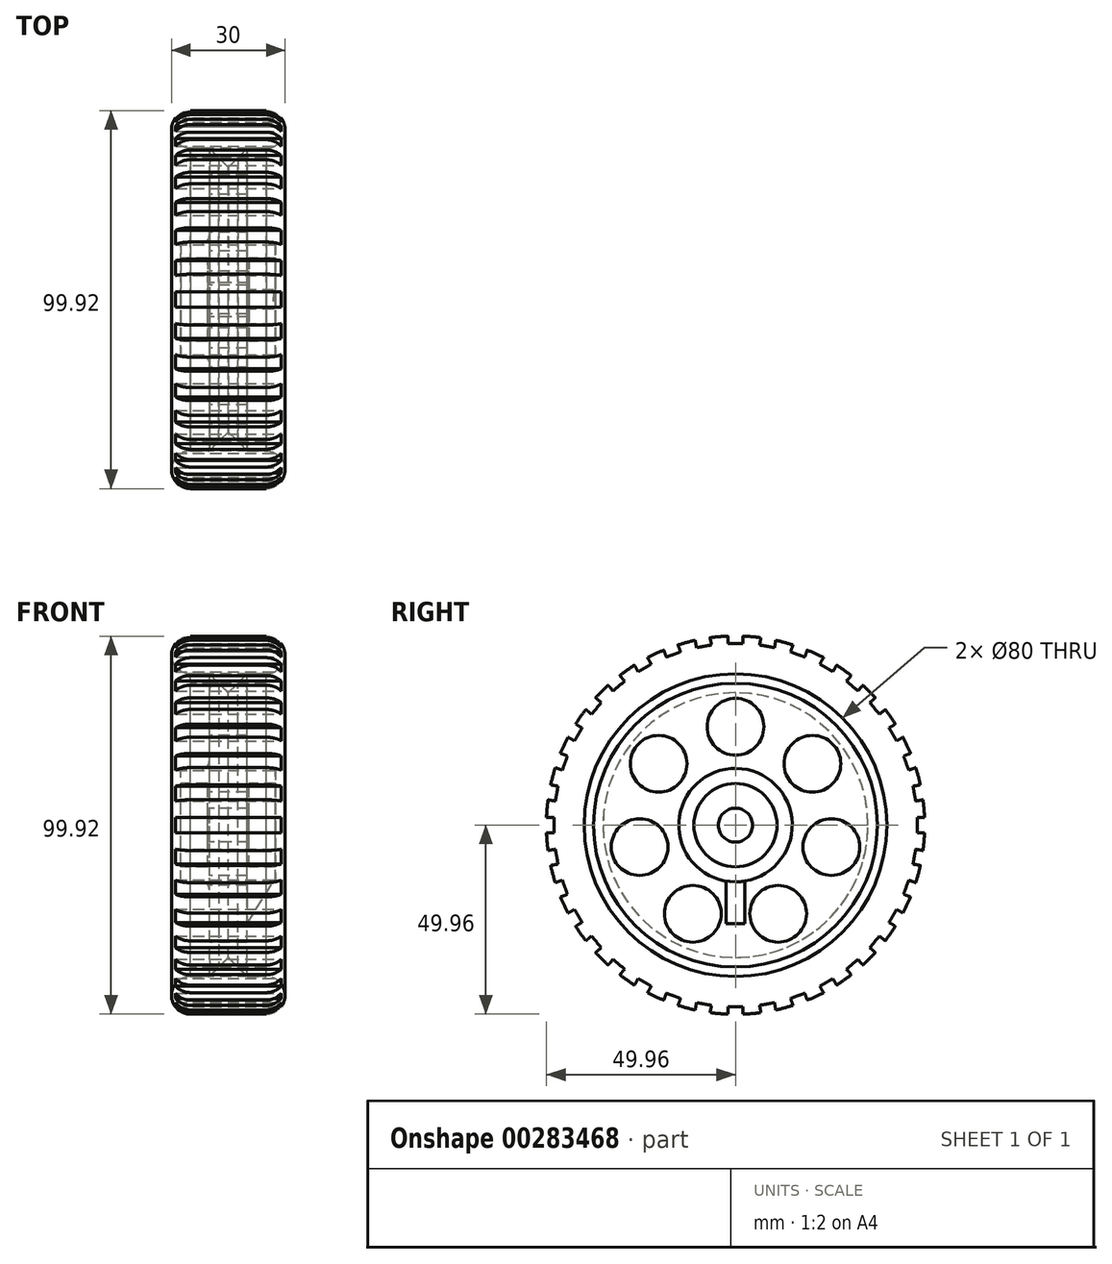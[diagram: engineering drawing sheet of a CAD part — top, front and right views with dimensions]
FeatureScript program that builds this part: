
annotation { "Feature Type Name" : "Feature", "Feature Type Description" : "" }
export const myFeature = defineFeature(function(context is Context, id is Id, definition is map)
    precondition{}
    {
        {
            var Q0;
            Q0=qCreatedBy(makeId("Right.planeOp"),FACE);
            var sketch = newSketch(context, id + "F0", { "sketchPlane" : qUnion([Q0])});
            skCircle(sketch, "E0", {"center": v(0, 0) * mm, "radius": 4.5 * mm});
            skCircle(sketch, "E1", {"center": v(0, 0) * mm, "radius": 11 * mm});
            skCircle(sketch, "E2", {"center": v(0, 0) * mm, "radius": 15 * mm});
            skCircle(sketch, "E3", {"center": v(0, 0) * mm, "radius": 37.5 * mm});
            skCircle(sketch, "E4", {"center": v(0, 0) * mm, "radius": 40 * mm});
            skCircle(sketch, "E5", {"center": v(0, 26) * mm, "radius": 7.5 * mm});
            skCircle(sketch, "E6.1.0", {"center": v(-20.33, 16.21) * mm, "radius": 7.5 * mm});
            skCircle(sketch, "E6.2.0", {"center": v(-25.35, -5.79) * mm, "radius": 7.5 * mm});
            skCircle(sketch, "E6.3.0", {"center": v(-11.28, -23.43) * mm, "radius": 7.5 * mm});
            skCircle(sketch, "E6.4.0", {"center": v(11.28, -23.43) * mm, "radius": 7.5 * mm});
            skCircle(sketch, "E7.1.5.0", {"center": v(25.35, -5.79) * mm, "radius": 7.5 * mm});
            skCircle(sketch, "E7.1.6.0", {"center": v(20.33, 16.21) * mm, "radius": 7.5 * mm});
            skCircle(sketch, "E8", {"center": v(0, 0) * mm, "radius": 26 * mm, "construction": true});
            skPoint(sketch, "E9", {"position": v(0, -26) * mm});
            skSolve(sketch);
        }
        {
            var Q0;
            Q0=makeQuery(id+"F0.imprint","IMPRINT",FACE,{"disambiguationData":[TD([[makeQuery(id+"F0.imprint","IMPRINT",EDGE,{"derivedFrom":sQuery(id+"F0.wireOp",EDGE,"E1")}),-1.0]])]});
            extrude(context, id + "F1", {"entities" : qUnion([Q0]), "endBound" : BoundingType.SYMMETRIC, "depth" : 25 * mm, "hasSecondDirection" : true, "secondDirectionOppositeDirection" : true, "secondDirectionDepth" : 10 * mm});
        }
        {
            var Q0;
            Q0=makeQuery(id+"F0.imprint","IMPRINT",FACE,{"disambiguationData":[TD([[makeQuery(id+"F0.imprint","IMPRINT",EDGE,{"derivedFrom":sQuery(id+"F0.wireOp",EDGE,"E3")}),-1.0]])]});
            extrude(context, id + "F2", {"entities" : qUnion([Q0]), "endBound" : BoundingType.SYMMETRIC, "depth" : 20 * mm});
        }
        {
            var Q0;
            Q0=makeQuery(id+"F0.imprint","IMPRINT",FACE,{"disambiguationData":[TD([[makeQuery(id+"F0.imprint","IMPRINT",EDGE,{"derivedFrom":sQuery(id+"F0.wireOp",EDGE,"E2")}),-1.0]])]});
            extrude(context, id + "F3", {"entities" : qUnion([Q0]), "depth" : 5 * mm, "hasSecondDirection" : true, "secondDirectionOppositeDirection" : true, "secondDirectionDepth" : 5 * mm});
        }
        {
            var Q0;
            Q0=makeQuery(id+"F0.imprint","IMPRINT",FACE,{"disambiguationData":[TD([[makeQuery(id+"F0.imprint","IMPRINT",EDGE,{"derivedFrom":sQuery(id+"F0.wireOp",EDGE,"E0")}),-1.0]])]});
            extrude(context, id + "F4", {"entities" : qUnion([Q0]), "operationType" : NewBodyOperationType.ADD, "endBound" : BoundingType.SYMMETRIC, "depth" : (25 - 14) * mm, "hasSecondDirection" : true, "secondDirectionOppositeDirection" : true, "secondDirectionDepth" : 3 * mm});
        }
        {
            var Q0;
            Q0=qCreatedBy(makeId("Front.planeOp"),FACE);
            var sketch = newSketch(context, id + "F5", { "sketchPlane" : qUnion([Q0])});
            skLineSegment(sketch, "E10", {"start": v(10, 50) * mm, "end": v(-10, 50) * mm});
            skArc(sketch, "E11", {"start": v(10, 50) * mm, "mid": v(15, 45) * mm, "end": v(10, 40) * mm});
            skArc(sketch, "E12", {"start": v(-10, 50) * mm, "mid": v(-15, 45) * mm, "end": v(-10, 40) * mm});
            skLineSegment(sketch, "E13", {"start": v(10, 40) * mm, "end": v(5, 40) * mm});
            skLineSegment(sketch, "E14", {"start": v(5, 40) * mm, "end": v(0, 35) * mm});
            skLineSegment(sketch, "E15", {"start": v(0, 35) * mm, "end": v(-5, 40) * mm});
            skLineSegment(sketch, "E16", {"start": v(-5, 40) * mm, "end": v(-10, 40) * mm});
            skLineSegment(sketch, "E17", {"start": v(15.37, 0) * mm, "end": v(-22.9, 0) * mm, "construction": true});
            skSolve(sketch);
        }
        {
            var Q0;
            Q0=makeQuery(id+"F5.imprint","IMPRINT",FACE,{"disambiguationData":[TD([[makeQuery(id+"F5.imprint","IMPRINT",EDGE,{"derivedFrom":sQuery(id+"F5.wireOp",EDGE,"E10")}),1.0]])]});
            var Q1;
            Q1=sQuery(id+"F5.wireOp",EDGE,"E17");
            revolve(context, id + "F6", {"entities" : qUnion([Q0]), "axis" : qUnion([Q1]), "revolveType" : RevolveType.FULL});
        }
        {
            var Q0;
            Q0=makeQuery(id+"F6.opRevolve","SWEPT_BODY",BODY,{"disambiguationData":[OSD([sQuery(id+"F5.wireOp",EDGE,"E10"),sQuery(id+"F5.wireOp",EDGE,"E11"),sQuery(id+"F5.wireOp",EDGE,"E12"),sQuery(id+"F5.wireOp",EDGE,"E13"),sQuery(id+"F5.wireOp",EDGE,"E14"),sQuery(id+"F5.wireOp",EDGE,"E15"),sQuery(id+"F5.wireOp",EDGE,"E16")])]});
            var Q1;
            Q1=makeQuery(id+"F3.opExtrude","SWEPT_BODY",BODY,{"disambiguationData":[OSD([sQuery(id+"F0.wireOp",EDGE,"E2"),sQuery(id+"F0.wireOp",EDGE,"E3"),sQuery(id+"F0.wireOp",EDGE,"E5"),sQuery(id+"F0.wireOp",EDGE,"E6.1.0"),sQuery(id+"F0.wireOp",EDGE,"E6.2.0"),sQuery(id+"F0.wireOp",EDGE,"E6.3.0"),sQuery(id+"F0.wireOp",EDGE,"E6.4.0"),sQuery(id+"F0.wireOp",EDGE,"E7.1.5.0"),sQuery(id+"F0.wireOp",EDGE,"E7.1.6.0")])]});
            booleanBodies(context, id + "F7", {"operationType" : BooleanOperationType.SUBTRACTION, "tools" : qUnion([Q0]), "targets" : qUnion([Q1]), "keepTools" : true});
        }
        {
            var Q0;
            Q0=qCreatedBy(makeId("Right.planeOp"),FACE);
            var sketch = newSketch(context, id + "F8", { "sketchPlane" : qUnion([Q0])});
            skLineSegment(sketch, "E18.bottom", {"start": v(2, 52) * mm, "end": v(-2, 52) * mm});
            skLineSegment(sketch, "E18.top", {"start": v(2, 48) * mm, "end": v(-2, 48) * mm});
            skLineSegment(sketch, "E18.left", {"start": v(2, 52) * mm, "end": v(2, 48) * mm});
            skLineSegment(sketch, "E18.right", {"start": v(-2, 52) * mm, "end": v(-2, 48) * mm});
            skPoint(sketch, "E18.middle", {"position": v(0, 50) * mm});
            skLineSegment(sketch, "E19.1.0", {"start": v(-7.06, 51.56) * mm, "end": v(-11, 50.86) * mm});
            skLineSegment(sketch, "E19.1.1", {"start": v(-7.06, 51.56) * mm, "end": v(-6.37, 47.62) * mm});
            skLineSegment(sketch, "E19.1.2", {"start": v(-6.37, 47.62) * mm, "end": v(-10.3, 46.92) * mm});
            skLineSegment(sketch, "E19.1.3", {"start": v(-11, 50.86) * mm, "end": v(-10.3, 46.92) * mm});
            skLineSegment(sketch, "E19.2.0", {"start": v(-15.9, 49.55) * mm, "end": v(-19.66, 48.18) * mm});
            skLineSegment(sketch, "E19.2.1", {"start": v(-15.9, 49.55) * mm, "end": v(-14.54, 45.79) * mm});
            skLineSegment(sketch, "E19.2.2", {"start": v(-14.54, 45.79) * mm, "end": v(-18.3, 44.42) * mm});
            skLineSegment(sketch, "E19.2.3", {"start": v(-19.66, 48.18) * mm, "end": v(-18.3, 44.42) * mm});
            skLineSegment(sketch, "E19.3.0", {"start": v(-24.27, 46.03) * mm, "end": v(-27.73, 44.03) * mm});
            skLineSegment(sketch, "E19.3.1", {"start": v(-24.27, 46.03) * mm, "end": v(-22.27, 42.57) * mm});
            skLineSegment(sketch, "E19.3.2", {"start": v(-22.27, 42.57) * mm, "end": v(-25.73, 40.57) * mm});
            skLineSegment(sketch, "E19.3.3", {"start": v(-27.73, 44.03) * mm, "end": v(-25.73, 40.57) * mm});
            skLineSegment(sketch, "E19.4.0", {"start": v(-31.9, 41.12) * mm, "end": v(-34.96, 38.55) * mm});
            skLineSegment(sketch, "E19.4.1", {"start": v(-31.9, 41.12) * mm, "end": v(-29.32, 38.06) * mm});
            skLineSegment(sketch, "E19.4.2", {"start": v(-29.32, 38.06) * mm, "end": v(-32.39, 35.48) * mm});
            skLineSegment(sketch, "E19.4.3", {"start": v(-34.96, 38.55) * mm, "end": v(-32.39, 35.48) * mm});
            skLineSegment(sketch, "E19.5.0", {"start": v(-38.55, 34.96) * mm, "end": v(-41.12, 31.9) * mm});
            skLineSegment(sketch, "E19.5.1", {"start": v(-38.55, 34.96) * mm, "end": v(-35.48, 32.39) * mm});
            skLineSegment(sketch, "E19.5.2", {"start": v(-35.48, 32.39) * mm, "end": v(-38.06, 29.32) * mm});
            skLineSegment(sketch, "E19.5.3", {"start": v(-41.12, 31.9) * mm, "end": v(-38.06, 29.32) * mm});
            skLineSegment(sketch, "E19.6.0", {"start": v(-44.03, 27.73) * mm, "end": v(-46.03, 24.27) * mm});
            skLineSegment(sketch, "E19.6.1", {"start": v(-44.03, 27.73) * mm, "end": v(-40.57, 25.73) * mm});
            skLineSegment(sketch, "E19.6.2", {"start": v(-40.57, 25.73) * mm, "end": v(-42.57, 22.27) * mm});
            skLineSegment(sketch, "E19.6.3", {"start": v(-46.03, 24.27) * mm, "end": v(-42.57, 22.27) * mm});
            skLineSegment(sketch, "E19.7.0", {"start": v(-48.18, 19.66) * mm, "end": v(-49.55, 15.9) * mm});
            skLineSegment(sketch, "E19.7.1", {"start": v(-48.18, 19.66) * mm, "end": v(-44.42, 18.3) * mm});
            skLineSegment(sketch, "E19.7.2", {"start": v(-44.42, 18.3) * mm, "end": v(-45.79, 14.54) * mm});
            skLineSegment(sketch, "E19.7.3", {"start": v(-49.55, 15.9) * mm, "end": v(-45.79, 14.54) * mm});
            skLineSegment(sketch, "E19.8.0", {"start": v(-50.86, 11) * mm, "end": v(-51.56, 7.06) * mm});
            skLineSegment(sketch, "E19.8.1", {"start": v(-50.86, 11) * mm, "end": v(-46.92, 10.3) * mm});
            skLineSegment(sketch, "E19.8.2", {"start": v(-46.92, 10.3) * mm, "end": v(-47.62, 6.37) * mm});
            skLineSegment(sketch, "E19.8.3", {"start": v(-51.56, 7.06) * mm, "end": v(-47.62, 6.37) * mm});
            skLineSegment(sketch, "E19.9.0", {"start": v(-52, 2) * mm, "end": v(-52, -2) * mm});
            skLineSegment(sketch, "E19.9.1", {"start": v(-52, 2) * mm, "end": v(-48, 2) * mm});
            skLineSegment(sketch, "E19.9.2", {"start": v(-48, 2) * mm, "end": v(-48, -2) * mm});
            skLineSegment(sketch, "E19.9.3", {"start": v(-52, -2) * mm, "end": v(-48, -2) * mm});
            skLineSegment(sketch, "E19.10.0", {"start": v(-51.56, -7.06) * mm, "end": v(-50.86, -11) * mm});
            skLineSegment(sketch, "E19.10.1", {"start": v(-51.56, -7.06) * mm, "end": v(-47.62, -6.37) * mm});
            skLineSegment(sketch, "E19.10.2", {"start": v(-47.62, -6.37) * mm, "end": v(-46.92, -10.3) * mm});
            skLineSegment(sketch, "E19.10.3", {"start": v(-50.86, -11) * mm, "end": v(-46.92, -10.3) * mm});
            skLineSegment(sketch, "E19.11.0", {"start": v(-49.55, -15.9) * mm, "end": v(-48.18, -19.66) * mm});
            skLineSegment(sketch, "E19.11.1", {"start": v(-49.55, -15.9) * mm, "end": v(-45.79, -14.54) * mm});
            skLineSegment(sketch, "E19.11.2", {"start": v(-45.79, -14.54) * mm, "end": v(-44.42, -18.3) * mm});
            skLineSegment(sketch, "E19.11.3", {"start": v(-48.18, -19.66) * mm, "end": v(-44.42, -18.3) * mm});
            skLineSegment(sketch, "E19.12.0", {"start": v(-46.03, -24.27) * mm, "end": v(-44.03, -27.73) * mm});
            skLineSegment(sketch, "E19.12.1", {"start": v(-46.03, -24.27) * mm, "end": v(-42.57, -22.27) * mm});
            skLineSegment(sketch, "E19.12.2", {"start": v(-42.57, -22.27) * mm, "end": v(-40.57, -25.73) * mm});
            skLineSegment(sketch, "E19.12.3", {"start": v(-44.03, -27.73) * mm, "end": v(-40.57, -25.73) * mm});
            skLineSegment(sketch, "E19.13.0", {"start": v(-41.12, -31.9) * mm, "end": v(-38.55, -34.96) * mm});
            skLineSegment(sketch, "E19.13.1", {"start": v(-41.12, -31.9) * mm, "end": v(-38.06, -29.32) * mm});
            skLineSegment(sketch, "E19.13.2", {"start": v(-38.06, -29.32) * mm, "end": v(-35.48, -32.39) * mm});
            skLineSegment(sketch, "E19.13.3", {"start": v(-38.55, -34.96) * mm, "end": v(-35.48, -32.39) * mm});
            skLineSegment(sketch, "E19.14.0", {"start": v(-34.96, -38.55) * mm, "end": v(-31.9, -41.12) * mm});
            skLineSegment(sketch, "E19.14.1", {"start": v(-34.96, -38.55) * mm, "end": v(-32.39, -35.48) * mm});
            skLineSegment(sketch, "E19.14.2", {"start": v(-32.39, -35.48) * mm, "end": v(-29.32, -38.06) * mm});
            skLineSegment(sketch, "E19.14.3", {"start": v(-31.9, -41.12) * mm, "end": v(-29.32, -38.06) * mm});
            skLineSegment(sketch, "E19.15.0", {"start": v(-27.73, -44.03) * mm, "end": v(-24.27, -46.03) * mm});
            skLineSegment(sketch, "E19.15.1", {"start": v(-27.73, -44.03) * mm, "end": v(-25.73, -40.57) * mm});
            skLineSegment(sketch, "E19.15.2", {"start": v(-25.73, -40.57) * mm, "end": v(-22.27, -42.57) * mm});
            skLineSegment(sketch, "E19.15.3", {"start": v(-24.27, -46.03) * mm, "end": v(-22.27, -42.57) * mm});
            skLineSegment(sketch, "E19.16.0", {"start": v(-19.66, -48.18) * mm, "end": v(-15.9, -49.55) * mm});
            skLineSegment(sketch, "E19.16.1", {"start": v(-19.66, -48.18) * mm, "end": v(-18.3, -44.42) * mm});
            skLineSegment(sketch, "E19.16.2", {"start": v(-18.3, -44.42) * mm, "end": v(-14.54, -45.79) * mm});
            skLineSegment(sketch, "E19.16.3", {"start": v(-15.9, -49.55) * mm, "end": v(-14.54, -45.79) * mm});
            skLineSegment(sketch, "E19.17.0", {"start": v(-11, -50.86) * mm, "end": v(-7.06, -51.56) * mm});
            skLineSegment(sketch, "E19.17.1", {"start": v(-11, -50.86) * mm, "end": v(-10.3, -46.92) * mm});
            skLineSegment(sketch, "E19.17.2", {"start": v(-10.3, -46.92) * mm, "end": v(-6.37, -47.62) * mm});
            skLineSegment(sketch, "E19.17.3", {"start": v(-7.06, -51.56) * mm, "end": v(-6.37, -47.62) * mm});
            skLineSegment(sketch, "E19.18.0", {"start": v(-2, -52) * mm, "end": v(2, -52) * mm});
            skLineSegment(sketch, "E19.18.1", {"start": v(-2, -52) * mm, "end": v(-2, -48) * mm});
            skLineSegment(sketch, "E19.18.2", {"start": v(-2, -48) * mm, "end": v(2, -48) * mm});
            skLineSegment(sketch, "E19.18.3", {"start": v(2, -52) * mm, "end": v(2, -48) * mm});
            skLineSegment(sketch, "E19.19.0", {"start": v(7.06, -51.56) * mm, "end": v(11, -50.86) * mm});
            skLineSegment(sketch, "E19.19.1", {"start": v(7.06, -51.56) * mm, "end": v(6.37, -47.62) * mm});
            skLineSegment(sketch, "E19.19.2", {"start": v(6.37, -47.62) * mm, "end": v(10.3, -46.92) * mm});
            skLineSegment(sketch, "E19.19.3", {"start": v(11, -50.86) * mm, "end": v(10.3, -46.92) * mm});
            skLineSegment(sketch, "E19.20.0", {"start": v(15.9, -49.55) * mm, "end": v(19.66, -48.18) * mm});
            skLineSegment(sketch, "E19.20.1", {"start": v(15.9, -49.55) * mm, "end": v(14.54, -45.79) * mm});
            skLineSegment(sketch, "E19.20.2", {"start": v(14.54, -45.79) * mm, "end": v(18.3, -44.42) * mm});
            skLineSegment(sketch, "E19.20.3", {"start": v(19.66, -48.18) * mm, "end": v(18.3, -44.42) * mm});
            skLineSegment(sketch, "E19.21.0", {"start": v(24.27, -46.03) * mm, "end": v(27.73, -44.03) * mm});
            skLineSegment(sketch, "E19.21.1", {"start": v(24.27, -46.03) * mm, "end": v(22.27, -42.57) * mm});
            skLineSegment(sketch, "E19.21.2", {"start": v(22.27, -42.57) * mm, "end": v(25.73, -40.57) * mm});
            skLineSegment(sketch, "E19.21.3", {"start": v(27.73, -44.03) * mm, "end": v(25.73, -40.57) * mm});
            skLineSegment(sketch, "E19.22.0", {"start": v(31.9, -41.12) * mm, "end": v(34.96, -38.55) * mm});
            skLineSegment(sketch, "E19.22.1", {"start": v(31.9, -41.12) * mm, "end": v(29.32, -38.06) * mm});
            skLineSegment(sketch, "E19.22.2", {"start": v(29.32, -38.06) * mm, "end": v(32.39, -35.48) * mm});
            skLineSegment(sketch, "E19.22.3", {"start": v(34.96, -38.55) * mm, "end": v(32.39, -35.48) * mm});
            skLineSegment(sketch, "E19.23.0", {"start": v(38.55, -34.96) * mm, "end": v(41.12, -31.9) * mm});
            skLineSegment(sketch, "E19.23.1", {"start": v(38.55, -34.96) * mm, "end": v(35.48, -32.39) * mm});
            skLineSegment(sketch, "E19.23.2", {"start": v(35.48, -32.39) * mm, "end": v(38.06, -29.32) * mm});
            skLineSegment(sketch, "E19.23.3", {"start": v(41.12, -31.9) * mm, "end": v(38.06, -29.32) * mm});
            skLineSegment(sketch, "E19.24.0", {"start": v(44.03, -27.73) * mm, "end": v(46.03, -24.27) * mm});
            skLineSegment(sketch, "E19.24.1", {"start": v(44.03, -27.73) * mm, "end": v(40.57, -25.73) * mm});
            skLineSegment(sketch, "E19.24.2", {"start": v(40.57, -25.73) * mm, "end": v(42.57, -22.27) * mm});
            skLineSegment(sketch, "E19.24.3", {"start": v(46.03, -24.27) * mm, "end": v(42.57, -22.27) * mm});
            skLineSegment(sketch, "E19.25.0", {"start": v(48.18, -19.66) * mm, "end": v(49.55, -15.9) * mm});
            skLineSegment(sketch, "E19.25.1", {"start": v(48.18, -19.66) * mm, "end": v(44.42, -18.3) * mm});
            skLineSegment(sketch, "E19.25.2", {"start": v(44.42, -18.3) * mm, "end": v(45.79, -14.54) * mm});
            skLineSegment(sketch, "E19.25.3", {"start": v(49.55, -15.9) * mm, "end": v(45.79, -14.54) * mm});
            skLineSegment(sketch, "E19.26.0", {"start": v(50.86, -11) * mm, "end": v(51.56, -7.06) * mm});
            skLineSegment(sketch, "E19.26.1", {"start": v(50.86, -11) * mm, "end": v(46.92, -10.3) * mm});
            skLineSegment(sketch, "E19.26.2", {"start": v(46.92, -10.3) * mm, "end": v(47.62, -6.37) * mm});
            skLineSegment(sketch, "E19.26.3", {"start": v(51.56, -7.06) * mm, "end": v(47.62, -6.37) * mm});
            skLineSegment(sketch, "E19.27.0", {"start": v(52, -2) * mm, "end": v(52, 2) * mm});
            skLineSegment(sketch, "E19.27.1", {"start": v(52, -2) * mm, "end": v(48, -2) * mm});
            skLineSegment(sketch, "E19.27.2", {"start": v(48, -2) * mm, "end": v(48, 2) * mm});
            skLineSegment(sketch, "E19.27.3", {"start": v(52, 2) * mm, "end": v(48, 2) * mm});
            skLineSegment(sketch, "E19.28.0", {"start": v(51.56, 7.06) * mm, "end": v(50.86, 11) * mm});
            skLineSegment(sketch, "E19.28.1", {"start": v(51.56, 7.06) * mm, "end": v(47.62, 6.37) * mm});
            skLineSegment(sketch, "E19.28.2", {"start": v(47.62, 6.37) * mm, "end": v(46.92, 10.3) * mm});
            skLineSegment(sketch, "E19.28.3", {"start": v(50.86, 11) * mm, "end": v(46.92, 10.3) * mm});
            skLineSegment(sketch, "E19.29.0", {"start": v(49.55, 15.9) * mm, "end": v(48.18, 19.66) * mm});
            skLineSegment(sketch, "E19.29.1", {"start": v(49.55, 15.9) * mm, "end": v(45.79, 14.54) * mm});
            skLineSegment(sketch, "E19.29.2", {"start": v(45.79, 14.54) * mm, "end": v(44.42, 18.3) * mm});
            skLineSegment(sketch, "E19.29.3", {"start": v(48.18, 19.66) * mm, "end": v(44.42, 18.3) * mm});
            skLineSegment(sketch, "E19.30.0", {"start": v(46.03, 24.27) * mm, "end": v(44.03, 27.73) * mm});
            skLineSegment(sketch, "E19.30.1", {"start": v(46.03, 24.27) * mm, "end": v(42.57, 22.27) * mm});
            skLineSegment(sketch, "E19.30.2", {"start": v(42.57, 22.27) * mm, "end": v(40.57, 25.73) * mm});
            skLineSegment(sketch, "E19.30.3", {"start": v(44.03, 27.73) * mm, "end": v(40.57, 25.73) * mm});
            skLineSegment(sketch, "E19.31.0", {"start": v(41.12, 31.9) * mm, "end": v(38.55, 34.96) * mm});
            skLineSegment(sketch, "E19.31.1", {"start": v(41.12, 31.9) * mm, "end": v(38.06, 29.32) * mm});
            skLineSegment(sketch, "E19.31.2", {"start": v(38.06, 29.32) * mm, "end": v(35.48, 32.39) * mm});
            skLineSegment(sketch, "E19.31.3", {"start": v(38.55, 34.96) * mm, "end": v(35.48, 32.39) * mm});
            skLineSegment(sketch, "E19.32.0", {"start": v(34.96, 38.55) * mm, "end": v(31.9, 41.12) * mm});
            skLineSegment(sketch, "E19.32.1", {"start": v(34.96, 38.55) * mm, "end": v(32.39, 35.48) * mm});
            skLineSegment(sketch, "E19.32.2", {"start": v(32.39, 35.48) * mm, "end": v(29.32, 38.06) * mm});
            skLineSegment(sketch, "E19.32.3", {"start": v(31.9, 41.12) * mm, "end": v(29.32, 38.06) * mm});
            skLineSegment(sketch, "E19.33.0", {"start": v(27.73, 44.03) * mm, "end": v(24.27, 46.03) * mm});
            skLineSegment(sketch, "E19.33.1", {"start": v(27.73, 44.03) * mm, "end": v(25.73, 40.57) * mm});
            skLineSegment(sketch, "E19.33.2", {"start": v(25.73, 40.57) * mm, "end": v(22.27, 42.57) * mm});
            skLineSegment(sketch, "E19.33.3", {"start": v(24.27, 46.03) * mm, "end": v(22.27, 42.57) * mm});
            skLineSegment(sketch, "E19.34.0", {"start": v(19.66, 48.18) * mm, "end": v(15.9, 49.55) * mm});
            skLineSegment(sketch, "E19.34.1", {"start": v(19.66, 48.18) * mm, "end": v(18.3, 44.42) * mm});
            skLineSegment(sketch, "E19.34.2", {"start": v(18.3, 44.42) * mm, "end": v(14.54, 45.79) * mm});
            skLineSegment(sketch, "E19.34.3", {"start": v(15.9, 49.55) * mm, "end": v(14.54, 45.79) * mm});
            skLineSegment(sketch, "E19.35.0", {"start": v(11, 50.86) * mm, "end": v(7.06, 51.56) * mm});
            skLineSegment(sketch, "E19.35.1", {"start": v(11, 50.86) * mm, "end": v(10.3, 46.92) * mm});
            skLineSegment(sketch, "E19.35.2", {"start": v(10.3, 46.92) * mm, "end": v(6.37, 47.62) * mm});
            skLineSegment(sketch, "E19.35.3", {"start": v(7.06, 51.56) * mm, "end": v(6.37, 47.62) * mm});
            skPoint(sketch, "E19.center", {"position": v(0, 0) * mm});
            skSolve(sketch);
        }
        {
            var Q0;
            Q0 = qSketchRegion(id + "F8", true);
            extrude(context, id + "F9", {"entities" : qUnion([Q0]), "operationType" : NewBodyOperationType.REMOVE, "endBound" : BoundingType.THROUGH_ALL, "oppositeDirection" : true, "depth" : 25 * mm, "hasSecondDirection" : true, "secondDirectionBound" : SecondDirectionBoundingType.THROUGH_ALL, "secondDirectionOppositeDirection" : false, "secondDirectionDepth" : 25 * mm});
        }
        {
            var Q0;
            Q0=qCreatedBy(makeId("Front.planeOp"),FACE);
            var sketch = newSketch(context, id + "F10", { "sketchPlane" : qUnion([Q0])});
            skLineSegment(sketch, "E20", {"start": v(5, -26) * mm, "end": v(12.5, -14) * mm});
            skLineSegment(sketch, "E21", {"start": v(12.5, -14) * mm, "end": v(5, -14) * mm});
            skLineSegment(sketch, "E22", {"start": v(5, -14) * mm, "end": v(5, -26) * mm});
            skLineSegment(sketch, "E23.0.0", {"start": v(12.5, 15) * mm, "end": v(12.5, -15) * mm});
            skLineSegment(sketch, "E24.0", {"start": v(12.5, 11) * mm, "end": v(12.5, -11) * mm});
            skSolve(sketch);
        }
        {
            var Q0;
            Q0 = qSketchRegion(id + "F10", true);
            extrude(context, id + "F11", {"entities" : qUnion([Q0]), "operationType" : NewBodyOperationType.ADD, "endBound" : BoundingType.SYMMETRIC, "depth" : 5 * mm});
        }
        {
            var Q0;
            Q0=makeQuery(id+"F3.opExtrude","CAP_EDGE",EDGE,{"disambiguationData":[OSD([sQuery(id+"F0.wireOp",EDGE,"E3")])],"isStart":false});
            var Q1;
            {var subQ0=sQuery(id+"F0.wireOp",EDGE,"E2");var subQ3=sQuery(id+"F10.wireOp",EDGE,"E22");var subQ4=sQuery(id+"F10.wireOp",EDGE,"E21");var subQ5=sQuery(id+"F10.wireOp",EDGE,"E20");var subQ6=makeQuery(id+"F11.opExtrude","CAP_FACE",FACE,{"disambiguationData":[OSD([subQ5,subQ4,subQ3])],"isStart":false});Q1=makeQuery(id+"FgzgCxp5MggecFg_4.6.F11.boolean.opBoolean","SPLIT",EDGE,{"disambiguationData":[TD([subQ6])],"derivedFrom":makeQuery(id+"FgzgCxp5MggecFg_4.5.F11.boolean.opBoolean","SPLIT",EDGE,{"disambiguationData":[TD([subQ6])],"derivedFrom":makeQuery(id+"FgzgCxp5MggecFg_4.4.F11.boolean.opBoolean","SPLIT",EDGE,{"disambiguationData":[TD([subQ6])],"derivedFrom":makeQuery(id+"FgzgCxp5MggecFg_4.3.F11.boolean.opBoolean","SPLIT",EDGE,{"disambiguationData":[TD([subQ6])],"derivedFrom":makeQuery(id+"FgzgCxp5MggecFg_4.2.F11.boolean.opBoolean","SPLIT",EDGE,{"disambiguationData":[TD([subQ6])],"derivedFrom":makeQuery(id+"FgzgCxp5MggecFg_4.1.F11.boolean.opBoolean","SPLIT",EDGE,{"disambiguationData":[TD([subQ6])],"derivedFrom":makeQuery(id+"F3.opExtrude","CAP_EDGE",EDGE,{"disambiguationData":[OSD([subQ0])],"isStart":false})})})})})})});}
            var Q2;
            {var subQ0=sQuery(id+"F0.wireOp",EDGE,"E2");var subQ2=sQuery(id+"F10.wireOp",EDGE,"E22");var subQ3=sQuery(id+"F10.wireOp",EDGE,"E21");var subQ4=sQuery(id+"F10.wireOp",EDGE,"E20");var subQ5=makeQuery(id+"FgzgCxp5MggecFg_4.5.F11.opExtrude","CAP_FACE",FACE,{"disambiguationData":[OSD([subQ4,subQ3,subQ2])],"isStart":true});var subQ7=makeQuery(id+"F11.opExtrude","CAP_FACE",FACE,{"disambiguationData":[OSD([subQ4,subQ3,subQ2])],"isStart":false});Q2=makeQuery(id+"FgzgCxp5MggecFg_4.6.F11.boolean.opBoolean","SPLIT",EDGE,{"disambiguationData":[TD([subQ5])],"derivedFrom":makeQuery(id+"FgzgCxp5MggecFg_4.5.F11.boolean.opBoolean","SPLIT",EDGE,{"disambiguationData":[TD([subQ7])],"derivedFrom":makeQuery(id+"FgzgCxp5MggecFg_4.4.F11.boolean.opBoolean","SPLIT",EDGE,{"disambiguationData":[TD([subQ7])],"derivedFrom":makeQuery(id+"FgzgCxp5MggecFg_4.3.F11.boolean.opBoolean","SPLIT",EDGE,{"disambiguationData":[TD([subQ7])],"derivedFrom":makeQuery(id+"FgzgCxp5MggecFg_4.2.F11.boolean.opBoolean","SPLIT",EDGE,{"disambiguationData":[TD([subQ7])],"derivedFrom":makeQuery(id+"FgzgCxp5MggecFg_4.1.F11.boolean.opBoolean","SPLIT",EDGE,{"disambiguationData":[TD([subQ7])],"derivedFrom":makeQuery(id+"F3.opExtrude","CAP_EDGE",EDGE,{"disambiguationData":[OSD([subQ0])],"isStart":false})})})})})})});}
            var Q3;
            {var subQ0=sQuery(id+"F0.wireOp",EDGE,"E2");var subQ1=sQuery(id+"F10.wireOp",EDGE,"E22");var subQ2=sQuery(id+"F10.wireOp",EDGE,"E21");var subQ3=sQuery(id+"F10.wireOp",EDGE,"E20");Q3=makeQuery(id+"FgzgCxp5MggecFg_4.1.F11.boolean.opBoolean","SPLIT",EDGE,{"disambiguationData":[TD([makeQuery(id+"F11.opExtrude","CAP_FACE",FACE,{"disambiguationData":[OSD([subQ3,subQ2,subQ1])],"isStart":true})])],"derivedFrom":makeQuery(id+"F3.opExtrude","CAP_EDGE",EDGE,{"disambiguationData":[OSD([subQ0])],"isStart":false})});}
            var Q4;
            {var subQ0=sQuery(id+"F0.wireOp",EDGE,"E2");var subQ2=sQuery(id+"F10.wireOp",EDGE,"E22");var subQ3=sQuery(id+"F10.wireOp",EDGE,"E21");var subQ4=sQuery(id+"F10.wireOp",EDGE,"E20");var subQ6=makeQuery(id+"FgzgCxp5MggecFg_4.1.F11.opExtrude","CAP_FACE",FACE,{"disambiguationData":[OSD([subQ4,subQ3,subQ2])],"isStart":true});Q4=makeQuery(id+"FgzgCxp5MggecFg_4.2.F11.boolean.opBoolean","SPLIT",EDGE,{"disambiguationData":[TD([subQ6])],"derivedFrom":makeQuery(id+"FgzgCxp5MggecFg_4.1.F11.boolean.opBoolean","SPLIT",EDGE,{"disambiguationData":[TD([makeQuery(id+"F11.opExtrude","CAP_FACE",FACE,{"disambiguationData":[OSD([subQ4,subQ3,subQ2])],"isStart":false})])],"derivedFrom":makeQuery(id+"F3.opExtrude","CAP_EDGE",EDGE,{"disambiguationData":[OSD([subQ0])],"isStart":false})})});}
            var Q5;
            {var subQ0=sQuery(id+"F0.wireOp",EDGE,"E2");var subQ3=sQuery(id+"F10.wireOp",EDGE,"E22");var subQ4=sQuery(id+"F10.wireOp",EDGE,"E21");var subQ5=sQuery(id+"F10.wireOp",EDGE,"E20");var subQ6=makeQuery(id+"FgzgCxp5MggecFg_4.2.F11.opExtrude","CAP_FACE",FACE,{"disambiguationData":[OSD([subQ5,subQ4,subQ3])],"isStart":true});var subQ7=makeQuery(id+"F11.opExtrude","CAP_FACE",FACE,{"disambiguationData":[OSD([subQ5,subQ4,subQ3])],"isStart":false});Q5=makeQuery(id+"FgzgCxp5MggecFg_4.3.F11.boolean.opBoolean","SPLIT",EDGE,{"disambiguationData":[TD([subQ6])],"derivedFrom":makeQuery(id+"FgzgCxp5MggecFg_4.2.F11.boolean.opBoolean","SPLIT",EDGE,{"disambiguationData":[TD([subQ7])],"derivedFrom":makeQuery(id+"FgzgCxp5MggecFg_4.1.F11.boolean.opBoolean","SPLIT",EDGE,{"disambiguationData":[TD([subQ7])],"derivedFrom":makeQuery(id+"F3.opExtrude","CAP_EDGE",EDGE,{"disambiguationData":[OSD([subQ0])],"isStart":false})})})});}
            var Q6;
            {var subQ0=sQuery(id+"F0.wireOp",EDGE,"E2");var subQ3=sQuery(id+"F10.wireOp",EDGE,"E22");var subQ4=sQuery(id+"F10.wireOp",EDGE,"E21");var subQ5=sQuery(id+"F10.wireOp",EDGE,"E20");var subQ6=makeQuery(id+"FgzgCxp5MggecFg_4.3.F11.opExtrude","CAP_FACE",FACE,{"disambiguationData":[OSD([subQ5,subQ4,subQ3])],"isStart":true});var subQ7=makeQuery(id+"F11.opExtrude","CAP_FACE",FACE,{"disambiguationData":[OSD([subQ5,subQ4,subQ3])],"isStart":false});Q6=makeQuery(id+"FgzgCxp5MggecFg_4.4.F11.boolean.opBoolean","SPLIT",EDGE,{"disambiguationData":[TD([subQ6])],"derivedFrom":makeQuery(id+"FgzgCxp5MggecFg_4.3.F11.boolean.opBoolean","SPLIT",EDGE,{"disambiguationData":[TD([subQ7])],"derivedFrom":makeQuery(id+"FgzgCxp5MggecFg_4.2.F11.boolean.opBoolean","SPLIT",EDGE,{"disambiguationData":[TD([subQ7])],"derivedFrom":makeQuery(id+"FgzgCxp5MggecFg_4.1.F11.boolean.opBoolean","SPLIT",EDGE,{"disambiguationData":[TD([subQ7])],"derivedFrom":makeQuery(id+"F3.opExtrude","CAP_EDGE",EDGE,{"disambiguationData":[OSD([subQ0])],"isStart":false})})})})});}
            var Q7;
            {var subQ0=sQuery(id+"F0.wireOp",EDGE,"E2");var subQ3=sQuery(id+"F10.wireOp",EDGE,"E22");var subQ4=sQuery(id+"F10.wireOp",EDGE,"E21");var subQ5=sQuery(id+"F10.wireOp",EDGE,"E20");var subQ6=makeQuery(id+"FgzgCxp5MggecFg_4.4.F11.opExtrude","CAP_FACE",FACE,{"disambiguationData":[OSD([subQ5,subQ4,subQ3])],"isStart":true});var subQ7=makeQuery(id+"F11.opExtrude","CAP_FACE",FACE,{"disambiguationData":[OSD([subQ5,subQ4,subQ3])],"isStart":false});Q7=makeQuery(id+"FgzgCxp5MggecFg_4.5.F11.boolean.opBoolean","SPLIT",EDGE,{"disambiguationData":[TD([subQ6])],"derivedFrom":makeQuery(id+"FgzgCxp5MggecFg_4.4.F11.boolean.opBoolean","SPLIT",EDGE,{"disambiguationData":[TD([subQ7])],"derivedFrom":makeQuery(id+"FgzgCxp5MggecFg_4.3.F11.boolean.opBoolean","SPLIT",EDGE,{"disambiguationData":[TD([subQ7])],"derivedFrom":makeQuery(id+"FgzgCxp5MggecFg_4.2.F11.boolean.opBoolean","SPLIT",EDGE,{"disambiguationData":[TD([subQ7])],"derivedFrom":makeQuery(id+"FgzgCxp5MggecFg_4.1.F11.boolean.opBoolean","SPLIT",EDGE,{"disambiguationData":[TD([subQ7])],"derivedFrom":makeQuery(id+"F3.opExtrude","CAP_EDGE",EDGE,{"disambiguationData":[OSD([subQ0])],"isStart":false})})})})})});}
            var Q8;
            Q8=makeQuery(id+"F3.opExtrude","CAP_EDGE",EDGE,{"disambiguationData":[OSD([sQuery(id+"F0.wireOp",EDGE,"E3")])],"isStart":true});
            var Q9;
            {var subQ0=sQuery(id+"F0.wireOp",EDGE,"E2");var subQ3=sQuery(id+"F10.wireOp",EDGE,"E22");var subQ4=sQuery(id+"F10.wireOp",EDGE,"E21");var subQ5=sQuery(id+"F10.wireOp",EDGE,"E20");var subQ6=makeQuery(id+"F2gH4dNI7RBgAhu_4.1.FgzgCxp5MggecFg_4.4.F11.opExtrude","CAP_FACE",FACE,{"disambiguationData":[OSD([subQ5,subQ4,subQ3])],"isStart":true});var subQ7=makeQuery(id+"F2gH4dNI7RBgAhu_4.1.F11.opExtrude","CAP_FACE",FACE,{"disambiguationData":[OSD([subQ5,subQ4,subQ3])],"isStart":false});Q9=makeQuery(id+"F2gH4dNI7RBgAhu_4.1.FgzgCxp5MggecFg_4.5.F11.boolean.opBoolean","SPLIT",EDGE,{"disambiguationData":[TD([subQ6])],"derivedFrom":makeQuery(id+"F2gH4dNI7RBgAhu_4.1.FgzgCxp5MggecFg_4.4.F11.boolean.opBoolean","SPLIT",EDGE,{"disambiguationData":[TD([subQ7])],"derivedFrom":makeQuery(id+"F2gH4dNI7RBgAhu_4.1.FgzgCxp5MggecFg_4.3.F11.boolean.opBoolean","SPLIT",EDGE,{"disambiguationData":[TD([subQ7])],"derivedFrom":makeQuery(id+"F2gH4dNI7RBgAhu_4.1.FgzgCxp5MggecFg_4.2.F11.boolean.opBoolean","SPLIT",EDGE,{"disambiguationData":[TD([subQ7])],"derivedFrom":makeQuery(id+"F2gH4dNI7RBgAhu_4.1.FgzgCxp5MggecFg_4.1.F11.boolean.opBoolean","SPLIT",EDGE,{"disambiguationData":[TD([subQ7])],"derivedFrom":makeQuery(id+"F3.opExtrude","CAP_EDGE",EDGE,{"disambiguationData":[OSD([subQ0])],"isStart":true})})})})})});}
            var Q10;
            {var subQ0=sQuery(id+"F0.wireOp",EDGE,"E2");var subQ3=sQuery(id+"F10.wireOp",EDGE,"E22");var subQ4=sQuery(id+"F10.wireOp",EDGE,"E21");var subQ5=sQuery(id+"F10.wireOp",EDGE,"E20");var subQ6=makeQuery(id+"F2gH4dNI7RBgAhu_4.1.FgzgCxp5MggecFg_4.5.F11.opExtrude","CAP_FACE",FACE,{"disambiguationData":[OSD([subQ5,subQ4,subQ3])],"isStart":true});var subQ7=makeQuery(id+"F2gH4dNI7RBgAhu_4.1.F11.opExtrude","CAP_FACE",FACE,{"disambiguationData":[OSD([subQ5,subQ4,subQ3])],"isStart":false});Q10=makeQuery(id+"F2gH4dNI7RBgAhu_4.1.FgzgCxp5MggecFg_4.6.F11.boolean.opBoolean","SPLIT",EDGE,{"disambiguationData":[TD([subQ6])],"derivedFrom":makeQuery(id+"F2gH4dNI7RBgAhu_4.1.FgzgCxp5MggecFg_4.5.F11.boolean.opBoolean","SPLIT",EDGE,{"disambiguationData":[TD([subQ7])],"derivedFrom":makeQuery(id+"F2gH4dNI7RBgAhu_4.1.FgzgCxp5MggecFg_4.4.F11.boolean.opBoolean","SPLIT",EDGE,{"disambiguationData":[TD([subQ7])],"derivedFrom":makeQuery(id+"F2gH4dNI7RBgAhu_4.1.FgzgCxp5MggecFg_4.3.F11.boolean.opBoolean","SPLIT",EDGE,{"disambiguationData":[TD([subQ7])],"derivedFrom":makeQuery(id+"F2gH4dNI7RBgAhu_4.1.FgzgCxp5MggecFg_4.2.F11.boolean.opBoolean","SPLIT",EDGE,{"disambiguationData":[TD([subQ7])],"derivedFrom":makeQuery(id+"F2gH4dNI7RBgAhu_4.1.FgzgCxp5MggecFg_4.1.F11.boolean.opBoolean","SPLIT",EDGE,{"disambiguationData":[TD([subQ7])],"derivedFrom":makeQuery(id+"F3.opExtrude","CAP_EDGE",EDGE,{"disambiguationData":[OSD([subQ0])],"isStart":true})})})})})})});}
            var Q11;
            {var subQ0=sQuery(id+"F0.wireOp",EDGE,"E2");var subQ3=sQuery(id+"F10.wireOp",EDGE,"E22");var subQ4=sQuery(id+"F10.wireOp",EDGE,"E21");var subQ5=sQuery(id+"F10.wireOp",EDGE,"E20");var subQ6=makeQuery(id+"F2gH4dNI7RBgAhu_4.1.F11.opExtrude","CAP_FACE",FACE,{"disambiguationData":[OSD([subQ5,subQ4,subQ3])],"isStart":false});Q11=makeQuery(id+"F2gH4dNI7RBgAhu_4.1.FgzgCxp5MggecFg_4.6.F11.boolean.opBoolean","SPLIT",EDGE,{"disambiguationData":[TD([subQ6])],"derivedFrom":makeQuery(id+"F2gH4dNI7RBgAhu_4.1.FgzgCxp5MggecFg_4.5.F11.boolean.opBoolean","SPLIT",EDGE,{"disambiguationData":[TD([subQ6])],"derivedFrom":makeQuery(id+"F2gH4dNI7RBgAhu_4.1.FgzgCxp5MggecFg_4.4.F11.boolean.opBoolean","SPLIT",EDGE,{"disambiguationData":[TD([subQ6])],"derivedFrom":makeQuery(id+"F2gH4dNI7RBgAhu_4.1.FgzgCxp5MggecFg_4.3.F11.boolean.opBoolean","SPLIT",EDGE,{"disambiguationData":[TD([subQ6])],"derivedFrom":makeQuery(id+"F2gH4dNI7RBgAhu_4.1.FgzgCxp5MggecFg_4.2.F11.boolean.opBoolean","SPLIT",EDGE,{"disambiguationData":[TD([subQ6])],"derivedFrom":makeQuery(id+"F2gH4dNI7RBgAhu_4.1.FgzgCxp5MggecFg_4.1.F11.boolean.opBoolean","SPLIT",EDGE,{"disambiguationData":[TD([subQ6])],"derivedFrom":makeQuery(id+"F3.opExtrude","CAP_EDGE",EDGE,{"disambiguationData":[OSD([subQ0])],"isStart":true})})})})})})});}
            var Q12;
            {var subQ0=sQuery(id+"F0.wireOp",EDGE,"E2");var subQ1=sQuery(id+"F10.wireOp",EDGE,"E22");var subQ2=sQuery(id+"F10.wireOp",EDGE,"E21");var subQ3=sQuery(id+"F10.wireOp",EDGE,"E20");Q12=makeQuery(id+"F2gH4dNI7RBgAhu_4.1.FgzgCxp5MggecFg_4.1.F11.boolean.opBoolean","SPLIT",EDGE,{"disambiguationData":[TD([makeQuery(id+"F2gH4dNI7RBgAhu_4.1.F11.opExtrude","CAP_FACE",FACE,{"disambiguationData":[OSD([subQ3,subQ2,subQ1])],"isStart":true})])],"derivedFrom":makeQuery(id+"F3.opExtrude","CAP_EDGE",EDGE,{"disambiguationData":[OSD([subQ0])],"isStart":true})});}
            var Q13;
            {var subQ0=sQuery(id+"F0.wireOp",EDGE,"E2");var subQ3=sQuery(id+"F10.wireOp",EDGE,"E22");var subQ4=sQuery(id+"F10.wireOp",EDGE,"E21");var subQ5=sQuery(id+"F10.wireOp",EDGE,"E20");var subQ6=makeQuery(id+"F2gH4dNI7RBgAhu_4.1.FgzgCxp5MggecFg_4.1.F11.opExtrude","CAP_FACE",FACE,{"disambiguationData":[OSD([subQ5,subQ4,subQ3])],"isStart":true});Q13=makeQuery(id+"F2gH4dNI7RBgAhu_4.1.FgzgCxp5MggecFg_4.2.F11.boolean.opBoolean","SPLIT",EDGE,{"disambiguationData":[TD([subQ6])],"derivedFrom":makeQuery(id+"F2gH4dNI7RBgAhu_4.1.FgzgCxp5MggecFg_4.1.F11.boolean.opBoolean","SPLIT",EDGE,{"disambiguationData":[TD([makeQuery(id+"F2gH4dNI7RBgAhu_4.1.F11.opExtrude","CAP_FACE",FACE,{"disambiguationData":[OSD([subQ5,subQ4,subQ3])],"isStart":false})])],"derivedFrom":makeQuery(id+"F3.opExtrude","CAP_EDGE",EDGE,{"disambiguationData":[OSD([subQ0])],"isStart":true})})});}
            var Q14;
            {var subQ0=sQuery(id+"F0.wireOp",EDGE,"E2");var subQ3=sQuery(id+"F10.wireOp",EDGE,"E22");var subQ4=sQuery(id+"F10.wireOp",EDGE,"E21");var subQ5=sQuery(id+"F10.wireOp",EDGE,"E20");var subQ6=makeQuery(id+"F2gH4dNI7RBgAhu_4.1.FgzgCxp5MggecFg_4.2.F11.opExtrude","CAP_FACE",FACE,{"disambiguationData":[OSD([subQ5,subQ4,subQ3])],"isStart":true});var subQ7=makeQuery(id+"F2gH4dNI7RBgAhu_4.1.F11.opExtrude","CAP_FACE",FACE,{"disambiguationData":[OSD([subQ5,subQ4,subQ3])],"isStart":false});Q14=makeQuery(id+"F2gH4dNI7RBgAhu_4.1.FgzgCxp5MggecFg_4.3.F11.boolean.opBoolean","SPLIT",EDGE,{"disambiguationData":[TD([subQ6])],"derivedFrom":makeQuery(id+"F2gH4dNI7RBgAhu_4.1.FgzgCxp5MggecFg_4.2.F11.boolean.opBoolean","SPLIT",EDGE,{"disambiguationData":[TD([subQ7])],"derivedFrom":makeQuery(id+"F2gH4dNI7RBgAhu_4.1.FgzgCxp5MggecFg_4.1.F11.boolean.opBoolean","SPLIT",EDGE,{"disambiguationData":[TD([subQ7])],"derivedFrom":makeQuery(id+"F3.opExtrude","CAP_EDGE",EDGE,{"disambiguationData":[OSD([subQ0])],"isStart":true})})})});}
            var Q15;
            {var subQ0=sQuery(id+"F0.wireOp",EDGE,"E2");var subQ3=sQuery(id+"F10.wireOp",EDGE,"E22");var subQ4=sQuery(id+"F10.wireOp",EDGE,"E21");var subQ5=sQuery(id+"F10.wireOp",EDGE,"E20");var subQ6=makeQuery(id+"F2gH4dNI7RBgAhu_4.1.FgzgCxp5MggecFg_4.3.F11.opExtrude","CAP_FACE",FACE,{"disambiguationData":[OSD([subQ5,subQ4,subQ3])],"isStart":true});var subQ7=makeQuery(id+"F2gH4dNI7RBgAhu_4.1.F11.opExtrude","CAP_FACE",FACE,{"disambiguationData":[OSD([subQ5,subQ4,subQ3])],"isStart":false});Q15=makeQuery(id+"F2gH4dNI7RBgAhu_4.1.FgzgCxp5MggecFg_4.4.F11.boolean.opBoolean","SPLIT",EDGE,{"disambiguationData":[TD([subQ6])],"derivedFrom":makeQuery(id+"F2gH4dNI7RBgAhu_4.1.FgzgCxp5MggecFg_4.3.F11.boolean.opBoolean","SPLIT",EDGE,{"disambiguationData":[TD([subQ7])],"derivedFrom":makeQuery(id+"F2gH4dNI7RBgAhu_4.1.FgzgCxp5MggecFg_4.2.F11.boolean.opBoolean","SPLIT",EDGE,{"disambiguationData":[TD([subQ7])],"derivedFrom":makeQuery(id+"F2gH4dNI7RBgAhu_4.1.FgzgCxp5MggecFg_4.1.F11.boolean.opBoolean","SPLIT",EDGE,{"disambiguationData":[TD([subQ7])],"derivedFrom":makeQuery(id+"F3.opExtrude","CAP_EDGE",EDGE,{"disambiguationData":[OSD([subQ0])],"isStart":true})})})})});}
            fillet(context, id + "F12", {"entities" : qUnion([Q0, Q1, Q2, Q3, Q4, Q5, Q6, Q7, Q8, Q9, Q10, Q11, Q12, Q13, Q14, Q15]), "radius" : 2 * mm, "tangentPropagation" : true, "allowEdgeOverflow" : false});
        }
    });
